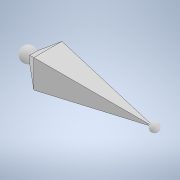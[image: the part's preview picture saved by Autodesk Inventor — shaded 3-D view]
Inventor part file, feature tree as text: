
AUTODESK INVENTOR PART (.ipt)
format: ipt  version: 2021 (Build 250183000, 183)  size: 150,528 bytes
history: native  units: mm
features: chamfer x6, sketch x5, extrude x3, other x2
ambient origin geometry x8: Origin, YZ Plane, XZ Plane, XY Plane, X Axis, Y Axis, Z Axis, Center Point
bodies: Body1 (feature_tree)
feature tree (16):
  extrude  "擠出3"  Depth=100.0mm
  chamfer  "倒角4"  Distance=450.0mm
  chamfer  "倒角5"  Distance=100.0mm
  chamfer  "倒角6"  Distance=50.0mm Angle=45.0deg
  chamfer  "倒角8"  Distance=70.0mm Angle=45.0deg
  chamfer  "倒角9"  Distance=70.0mm Angle=45.0deg
  chamfer  "倒角10"  Distance=50.0mm Angle=45.0deg
  extrude  "擠出4"  Depth=380.0mm TaperAngle=45.0deg
  extrude  "擠出5"  Depth=50.0mm TaperAngle=45.0deg
  other  "迴轉1"
  other  "迴轉2"
  sketch  "草圖3"
  sketch  "草圖4"
  sketch  "草圖5"
  sketch  "草圖6"
  sketch  "草圖7"
